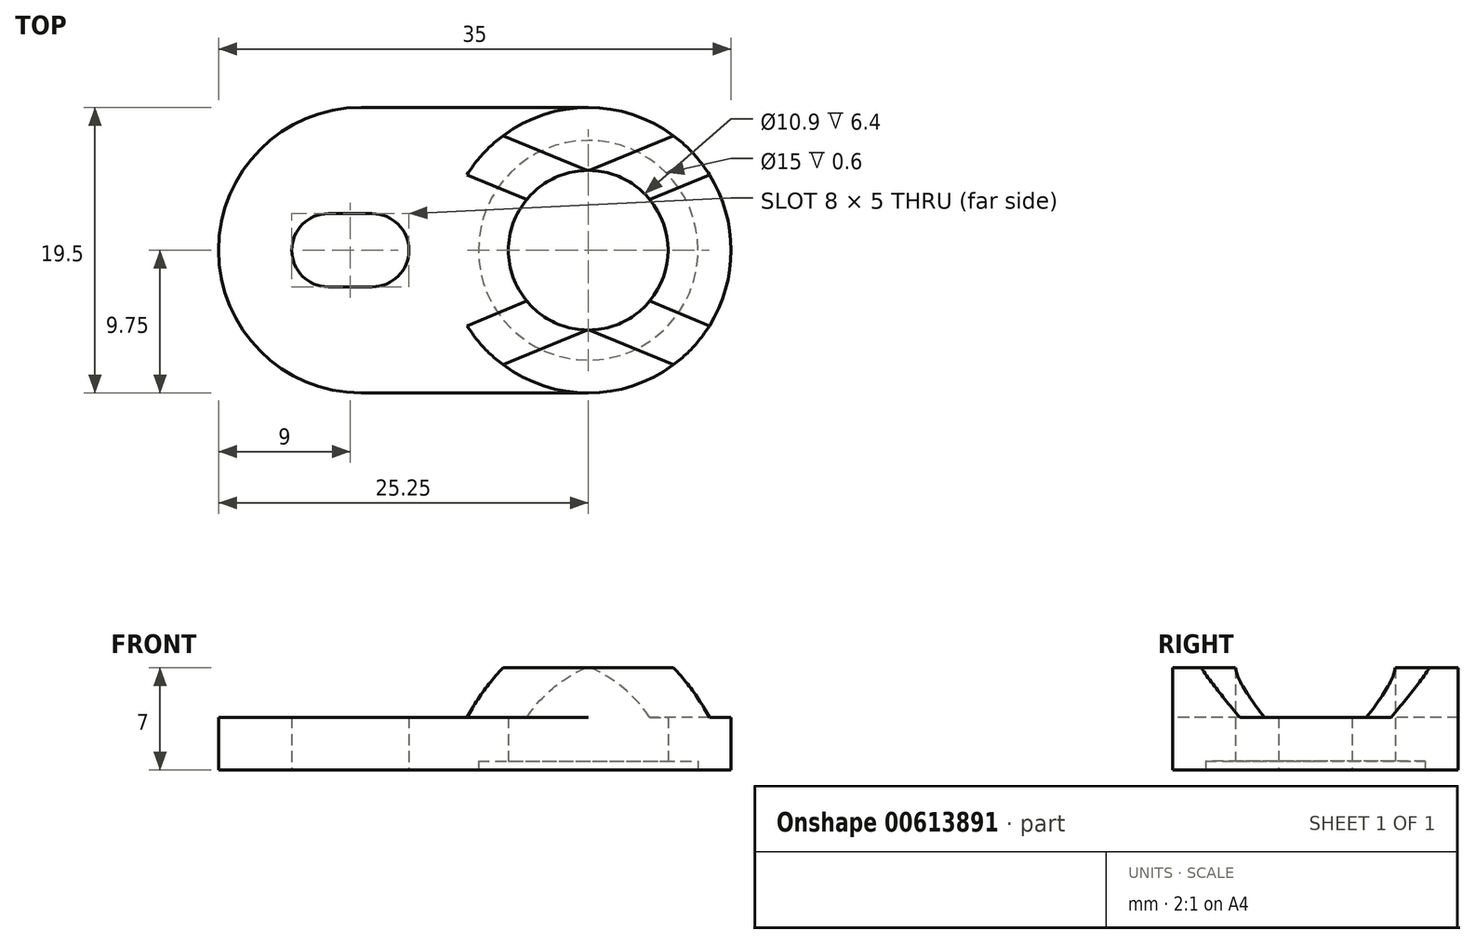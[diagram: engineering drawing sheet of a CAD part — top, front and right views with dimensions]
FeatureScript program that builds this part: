
annotation { "Feature Type Name" : "Feature", "Feature Type Description" : "" }
export const myFeature = defineFeature(function(context is Context, id is Id, definition is map)
    precondition{}
    {
        {
            var Q0;
            Q0=qCreatedBy(makeId("Top.planeOp"),FACE);
            var sketch = newSketch(context, id + "F0", { "sketchPlane" : qUnion([Q0])});
            skLineSegment(sketch, "E0.bottom", {"start": v(-0.25, 9.75) * mm, "end": v(15.25, 9.75) * mm});
            skLineSegment(sketch, "E0.top", {"start": v(-0.25, -9.75) * mm, "end": v(15.25, -9.75) * mm});
            skLineSegment(sketch, "E0.left", {"start": v(-10, 0) * mm, "end": v(-10, 0) * mm});
            skLineSegment(sketch, "E0.right", {"start": v(25, 0) * mm, "end": v(25, 0) * mm});
            skPoint(sketch, "E1.visualSharp", {"position": v(-10, 9.75) * mm});
            skArc(sketch, "E1.filletArc", {"start": v(-0.25, 9.75) * mm, "mid": v(-7.14, 6.9) * mm, "end": v(-10, 0) * mm});
            skPoint(sketch, "E2.visualSharp", {"position": v(-10, -9.75) * mm});
            skArc(sketch, "E2.filletArc", {"start": v(-10, 0) * mm, "mid": v(-7.14, -6.9) * mm, "end": v(-0.25, -9.75) * mm});
            skPoint(sketch, "E3.visualSharp", {"position": v(25, 9.75) * mm});
            skArc(sketch, "E3.filletArc", {"start": v(25, 0) * mm, "mid": v(22.14, 6.9) * mm, "end": v(15.25, 9.75) * mm});
            skPoint(sketch, "E4.visualSharp", {"position": v(25, -9.75) * mm});
            skArc(sketch, "E4.filletArc", {"start": v(15.25, -9.75) * mm, "mid": v(22.14, -6.9) * mm, "end": v(25, 0) * mm});
            skCircle(sketch, "E5", {"center": v(15.25, 0) * mm, "radius": 5.45 * mm});
            skArc(sketch, "E6", {"start": v(-2.5, 2.5) * mm, "mid": v(-5, 0) * mm, "end": v(-2.5, -2.5) * mm});
            skArc(sketch, "E7", {"start": v(0.5, -2.5) * mm, "mid": v(3, 0) * mm, "end": v(0.5, 2.5) * mm});
            skLineSegment(sketch, "E8", {"start": v(-2.5, 2.5) * mm, "end": v(0.5, 2.5) * mm});
            skLineSegment(sketch, "E9", {"start": v(0.5, -2.5) * mm, "end": v(-2.5, -2.5) * mm});
            skLineSegment(sketch, "E10.bottom", {"start": v(25, 9.75) * mm, "end": v(5.5, 9.75) * mm, "construction": true});
            skLineSegment(sketch, "E10.top", {"start": v(25, -9.75) * mm, "end": v(5.5, -9.75) * mm, "construction": true});
            skLineSegment(sketch, "E10.left", {"start": v(25, 9.75) * mm, "end": v(25, -9.75) * mm, "construction": true});
            skLineSegment(sketch, "E10.right", {"start": v(5.5, 9.75) * mm, "end": v(5.5, -9.75) * mm, "construction": true});
            skSolve(sketch);
        }
        {
            var Q0;
            Q0=makeQuery(id+"F0.imprint","IMPRINT",FACE,{"disambiguationData":[TD([[makeQuery(id+"F0.imprint","IMPRINT",EDGE,{"derivedFrom":sQuery(id+"F0.wireOp",EDGE,"E0.bottom")}),-1.0]])]});
            extrude(context, id + "F1", {"entities" : qUnion([Q0]), "depth" : 3.6 * mm, "offsetDistance" : 25 * mm});
        }
        {
            var Q0;
            Q0=makeQuery(id+"F1.opExtrude","CAP_FACE",FACE,{"disambiguationData":[OSD([sQuery(id+"F0.wireOp",EDGE,"E0.bottom"),sQuery(id+"F0.wireOp",EDGE,"E0.top"),sQuery(id+"F0.wireOp",EDGE,"E1.filletArc"),sQuery(id+"F0.wireOp",EDGE,"E2.filletArc"),sQuery(id+"F0.wireOp",EDGE,"E3.filletArc"),sQuery(id+"F0.wireOp",EDGE,"E4.filletArc"),sQuery(id+"F0.wireOp",EDGE,"E5"),sQuery(id+"F0.wireOp",EDGE,"E6"),sQuery(id+"F0.wireOp",EDGE,"E7"),sQuery(id+"F0.wireOp",EDGE,"E8"),sQuery(id+"F0.wireOp",EDGE,"E9")])],"isStart":false});
            var sketch = newSketch(context, id + "F2", { "sketchPlane" : qUnion([Q0])});
            skArc(sketch, "E11", {"start": v(10.21, -2.09) * mm, "mid": v(15.25, -5.45) * mm, "end": v(20.29, -2.09) * mm});
            skArc(sketch, "E12", {"start": v(6.24, -3.73) * mm, "mid": v(15.25, -9.75) * mm, "end": v(24.26, -3.73) * mm});
            skLineSegment(sketch, "E13", {"start": v(15.25, 0) * mm, "end": v(3.92, 11.33) * mm, "construction": true});
            skLineSegment(sketch, "E14", {"start": v(10.21, 2.09) * mm, "end": v(6.24, 3.73) * mm});
            skLineSegment(sketch, "E15", {"start": v(15.25, 0) * mm, "end": v(15.25, 3.82) * mm, "construction": true});
            skLineSegment(sketch, "E16.MirrorCS", {"start": v(20.29, 2.09) * mm, "end": v(24.26, 3.73) * mm});
            skLineSegment(sketch, "E17.MirrorCS", {"start": v(10.21, -2.09) * mm, "end": v(6.24, -3.73) * mm});
            skLineSegment(sketch, "E18.MirrorCS", {"start": v(20.29, -2.09) * mm, "end": v(24.26, -3.73) * mm});
            skArc(sketch, "E19.trimOffspring", {"start": v(24.26, 3.73) * mm, "mid": v(15.25, 9.75) * mm, "end": v(6.24, 3.73) * mm});
            skArc(sketch, "E20.trimOffspring", {"start": v(20.29, 2.09) * mm, "mid": v(15.25, 5.45) * mm, "end": v(10.21, 2.09) * mm});
            skSolve(sketch);
        }
        {
            var Q0;
            {var subQ2=sQuery(id+"F2.wireOp",EDGE,"E14");Q0=makeQuery(id+"F2.imprint","IMPRINT",FACE,{"disambiguationData":[TD([[makeQuery(id+"F2.imprint","IMPRINT",EDGE,{"derivedFrom":subQ2}),-1.0]])]});}
            var Q1;
            Q1=makeQuery(id+"F2.imprint","IMPRINT",FACE,{"disambiguationData":[TD([[makeQuery(id+"F2.imprint","IMPRINT",EDGE,{"derivedFrom":sQuery(id+"F2.wireOp",EDGE,"E11")}),-1.0]])]});
            extrude(context, id + "F3", {"entities" : qUnion([Q0, Q1]), "operationType" : NewBodyOperationType.ADD, "depth" : 3.4 * mm, "offsetDistance" : 25 * mm});
        }
        {
            var Q0;
            Q0=makeQuery(id+"F3.opExtrude","CAP_EDGE",EDGE,{"disambiguationData":[OSD([sQuery(id+"F2.wireOp",EDGE,"E14")])],"isStart":false});
            chamfer(context, id + "F4", {"entities" : qUnion([Q0]), "chamferType" : ChamferType.OFFSET_ANGLE, "width" : 5 * mm, "oppositeDirection" : false, "angle" : 45 * degree});
        }
        {
            var Q0;
            Q0=makeQuery(id+"F3.opExtrude","CAP_EDGE",EDGE,{"disambiguationData":[OSD([sQuery(id+"F2.wireOp",EDGE,"E16.MirrorCS")])],"isStart":false});
            chamfer(context, id + "F5", {"entities" : qUnion([Q0]), "width" : 5 * mm, "tangentPropagation" : true});
        }
        {
            var Q0;
            Q0=makeQuery(id+"F3.opExtrude","CAP_EDGE",EDGE,{"disambiguationData":[OSD([sQuery(id+"F2.wireOp",EDGE,"E18.MirrorCS")])],"isStart":false});
            chamfer(context, id + "F6", {"entities" : qUnion([Q0]), "width" : 5 * mm, "tangentPropagation" : true});
        }
        {
            var Q0;
            Q0=makeQuery(id+"F3.opExtrude","CAP_EDGE",EDGE,{"disambiguationData":[OSD([sQuery(id+"F2.wireOp",EDGE,"E17.MirrorCS")])],"isStart":false});
            chamfer(context, id + "F7", {"entities" : qUnion([Q0]), "width" : 5 * mm, "tangentPropagation" : true});
        }
        {
            var Q0;
            Q0=makeQuery(id+"F1.opExtrude","CAP_FACE",FACE,{"disambiguationData":[OSD([sQuery(id+"F0.wireOp",EDGE,"E0.bottom"),sQuery(id+"F0.wireOp",EDGE,"E0.top"),sQuery(id+"F0.wireOp",EDGE,"E1.filletArc"),sQuery(id+"F0.wireOp",EDGE,"E2.filletArc"),sQuery(id+"F0.wireOp",EDGE,"E3.filletArc"),sQuery(id+"F0.wireOp",EDGE,"E4.filletArc"),sQuery(id+"F0.wireOp",EDGE,"E5"),sQuery(id+"F0.wireOp",EDGE,"E6"),sQuery(id+"F0.wireOp",EDGE,"E7"),sQuery(id+"F0.wireOp",EDGE,"E8"),sQuery(id+"F0.wireOp",EDGE,"E9")])],"isStart":true});
            var sketch = newSketch(context, id + "F8", { "sketchPlane" : qUnion([Q0])});
            skCircle(sketch, "E21", {"center": v(15.25, 0) * mm, "radius": 7.5 * mm});
            skSolve(sketch);
        }
        {
            var Q0;
            Q0 = qSketchRegion(id + "F8", true);
            extrude(context, id + "F9", {"entities" : qUnion([Q0]), "operationType" : NewBodyOperationType.REMOVE, "oppositeDirection" : true, "depth" : 0.6 * mm, "offsetDistance" : 25 * mm});
        }
    });
